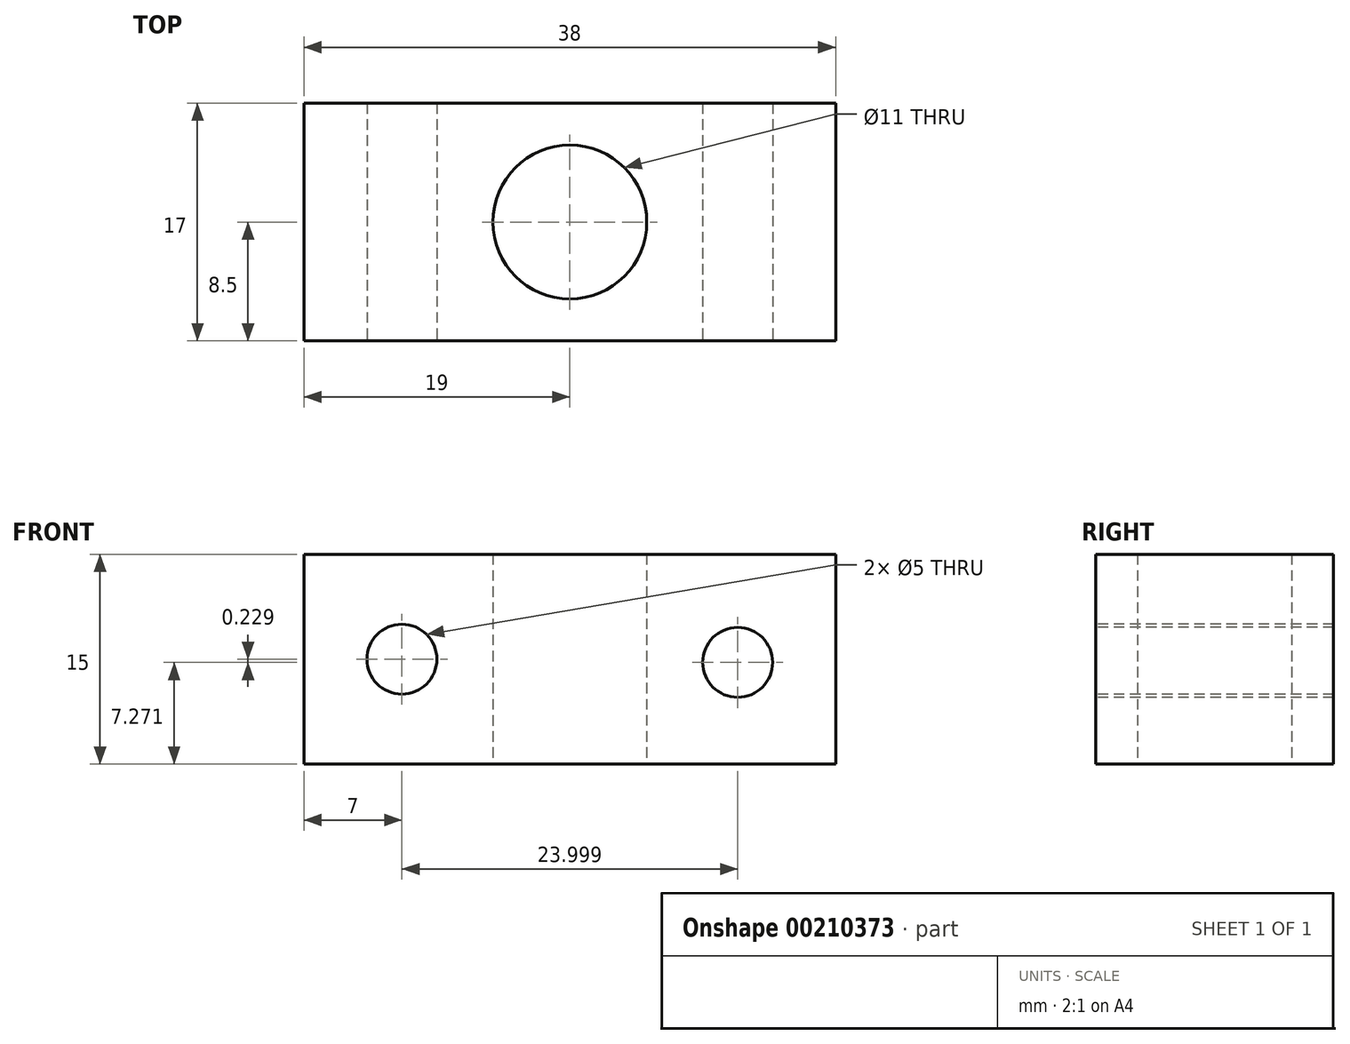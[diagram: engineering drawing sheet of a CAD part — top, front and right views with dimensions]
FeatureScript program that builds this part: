
annotation { "Feature Type Name" : "Feature", "Feature Type Description" : "" }
export const myFeature = defineFeature(function(context is Context, id is Id, definition is map)
    precondition{}
    {
        {
            var Q0;
            Q0=qCreatedBy(makeId("Top.planeOp"),FACE);
            var sketch = newSketch(context, id + "F0", { "sketchPlane" : qUnion([Q0])});
            skLineSegment(sketch, "E0.bottom", {"start": v(19, 8.5) * mm, "end": v(-19, 8.5) * mm});
            skLineSegment(sketch, "E0.top", {"start": v(19, -8.5) * mm, "end": v(-19, -8.5) * mm});
            skLineSegment(sketch, "E0.left", {"start": v(19, 8.5) * mm, "end": v(19, -8.5) * mm});
            skLineSegment(sketch, "E0.right", {"start": v(-19, 8.5) * mm, "end": v(-19, -8.5) * mm});
            skPoint(sketch, "E0.middle", {"position": v(0, 0) * mm});
            skSolve(sketch);
        }
        {
            var Q0;
            Q0 = qSketchRegion(id + "F0", true);
            extrude(context, id + "F1", {"entities" : qUnion([Q0]), "depth" : 15 * mm});
        }
        {
            var Q0;
            Q0=makeQuery(id+"F1.opExtrude","CAP_FACE",FACE,{"disambiguationData":[OSD([sQuery(id+"F0.wireOp",EDGE,"E0.bottom"),sQuery(id+"F0.wireOp",EDGE,"E0.top"),sQuery(id+"F0.wireOp",EDGE,"E0.left"),sQuery(id+"F0.wireOp",EDGE,"E0.right")])],"isStart":true});
            var sketch = newSketch(context, id + "F2", { "sketchPlane" : qUnion([Q0])});
            skPoint(sketch, "E1", {"position": v(0, 0) * mm});
            skSolve(sketch);
        }
        {
            var Q0;
            Q0=sQuery(id+"F2.wireOp",VERTEX,"E1");
            var Q1;
            Q1=makeQuery(id+"F1.opExtrude","SWEPT_BODY",BODY,{"disambiguationData":[OSD([sQuery(id+"F0.wireOp",EDGE,"E0.bottom"),sQuery(id+"F0.wireOp",EDGE,"E0.top"),sQuery(id+"F0.wireOp",EDGE,"E0.left"),sQuery(id+"F0.wireOp",EDGE,"E0.right")])]});
            hole(context, id + "F3", {"style" : HoleStyle.SIMPLE, "endStyle" : HoleEndStyle.THROUGH, "holeDiameter" : 11 * mm, "locations" : qUnion([Q0]), "scope" : qUnion([Q1]), "isTappedThrough" : true});
        }
        {
            var Q0;
            Q0=makeQuery(id+"F1.opExtrude","SWEPT_FACE",FACE,{"disambiguationData":[OSD([sQuery(id+"F0.wireOp",EDGE,"E0.top")])]});
            var sketch = newSketch(context, id + "F4", { "sketchPlane" : qUnion([Q0])});
            skPoint(sketch, "E2", {"position": v(-12, 7.5) * mm});
            skPoint(sketch, "E3", {"position": v(12, 7.27) * mm});
            skSolve(sketch);
        }
        {
            var Q0;
            Q0=sQuery(id+"F4.wireOp",VERTEX,"E2");
            var Q1;
            Q1=sQuery(id+"F4.wireOp",VERTEX,"E3");
            var Q2;
            Q2=makeQuery(id+"F1.opExtrude","SWEPT_BODY",BODY,{"disambiguationData":[OSD([sQuery(id+"F0.wireOp",EDGE,"E0.bottom"),sQuery(id+"F0.wireOp",EDGE,"E0.top"),sQuery(id+"F0.wireOp",EDGE,"E0.left"),sQuery(id+"F0.wireOp",EDGE,"E0.right")])]});
            hole(context, id + "F5", {"style" : HoleStyle.SIMPLE, "endStyle" : HoleEndStyle.THROUGH, "holeDiameter" : 5 * mm, "locations" : qUnion([Q0, Q1]), "scope" : qUnion([Q2]), "isTappedThrough" : true});
        }
    });
